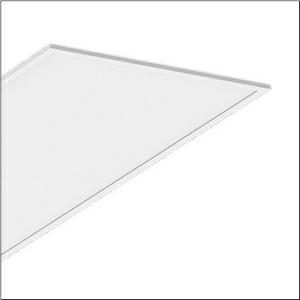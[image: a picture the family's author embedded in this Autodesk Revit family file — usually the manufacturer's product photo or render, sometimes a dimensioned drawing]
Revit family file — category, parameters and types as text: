
# Revit family: apollon_21_linear_51mq19wd2m14
name_source: partatom
category: Lighting Fixtures
units: mm (PartAtom-declared; Revit-internal decimal feet)

## family parameters
Cut with Voids When Loaded = No
Host = Face
Light Source = No
Part Type = Normal
Room Calculation Point = No
Round Connector Dimension = Use Diameter
Shared = No

## types (1)
- --- (1 x LED, 7000 lm, 44.6 W, 4000K)
    Apparent Load = 45 VA
    CIE Flux Codes = 60 87 97 100 100
    Color Rendering = 80
    Color Temperature = 4000K
    Default Elevation = 1800 mm
    Description = Apollon 21 linear, office luminaire, primary optical cover: micro prismatic cover, of PMMA, CAT 2 (L<= 3000cd/m²), light emission: direct distribution, primary light characteristic: symmetric, installation type: lay-in mounting, LED, rated luminous flux: 7.820lm, luminous efficacy: 173lm/W, light colour: 830/840, colour temperature: 3000/4000K, control gear: DALI 2, Multilumen, with terminal, 5-pole, mains connection: 220..240V, AC/DC, 0/50..60Hz, rated input power: 45.3W, housing, of aluminium, coated, traffic white (RAL 9016), length: 1.245mm, width: 622mm, height: 55mm, recess depth: 180mm, housing upper side, of sheet steel, galvanised, protection rating (complete): IP20, protection rating (lamp compartment, on room side): IP50, insulation class (complete): insulation class II (safety insulation), certification: CE, ENEC, impact resistance: IK03, permissible operating ambient temperature: -20..+45°C, permissible storage temperature: -40..+80°C, standard: EN 60598-2-22, packaging unit: 1 piece
    Height = 0 mm  [stored 0 ft]
    Lamp = 1 x LED
    Lamp Light Flux = 7000 lm
    Lamp Power = 44.6 W
    Lamp count = 1
    Length = 1245 mm
    Luminous efficacy = 157 lm/W
    Manufacturer = Siteco
    ModVariant = No
    Model = 51MQ19WD2M14
    Mounting Place = Ceiling
    Mounting Type = Recessed
    Number of Poles = 1
    OnlyDefault = Yes
    Power Factor = 1
    Product Name = Apollon 21 linear
    Product group = office luminaire | ceiling recessed
    ProductGroupID = 401
    Protection Class = Protection class II
    Protection Degree = IP 20
    RLX_Detail_Level = 1
    RLX_Emergency_Light_Flux = 0 lm
    RLX_Emergency_Type = 0
    RLX_Emergency_Type_DB = No
    RlxData = <blob elided: 19561 chars, md5=995d7ee5>
    Socket = socket
    Standby Power = 0 W
    System Light Flux = 7000 lm
    System Power = 45 W
    Type Comments = factory setting
    Type Image = l_1335551.jpg
    URL = http://relux.com
    VarID = @adj_068392
    Voltage = 0 V
    Weight = 0.00 kg
    Width = 622 mm

note: [stored X ft] marks values corroborated as IEEE doubles in the binary element streams (Revit-internal decimal feet)

## geometry (parser evidence)
native form markers: Blend x4, Sweep x9
no freeform markers — native parametric forms only
